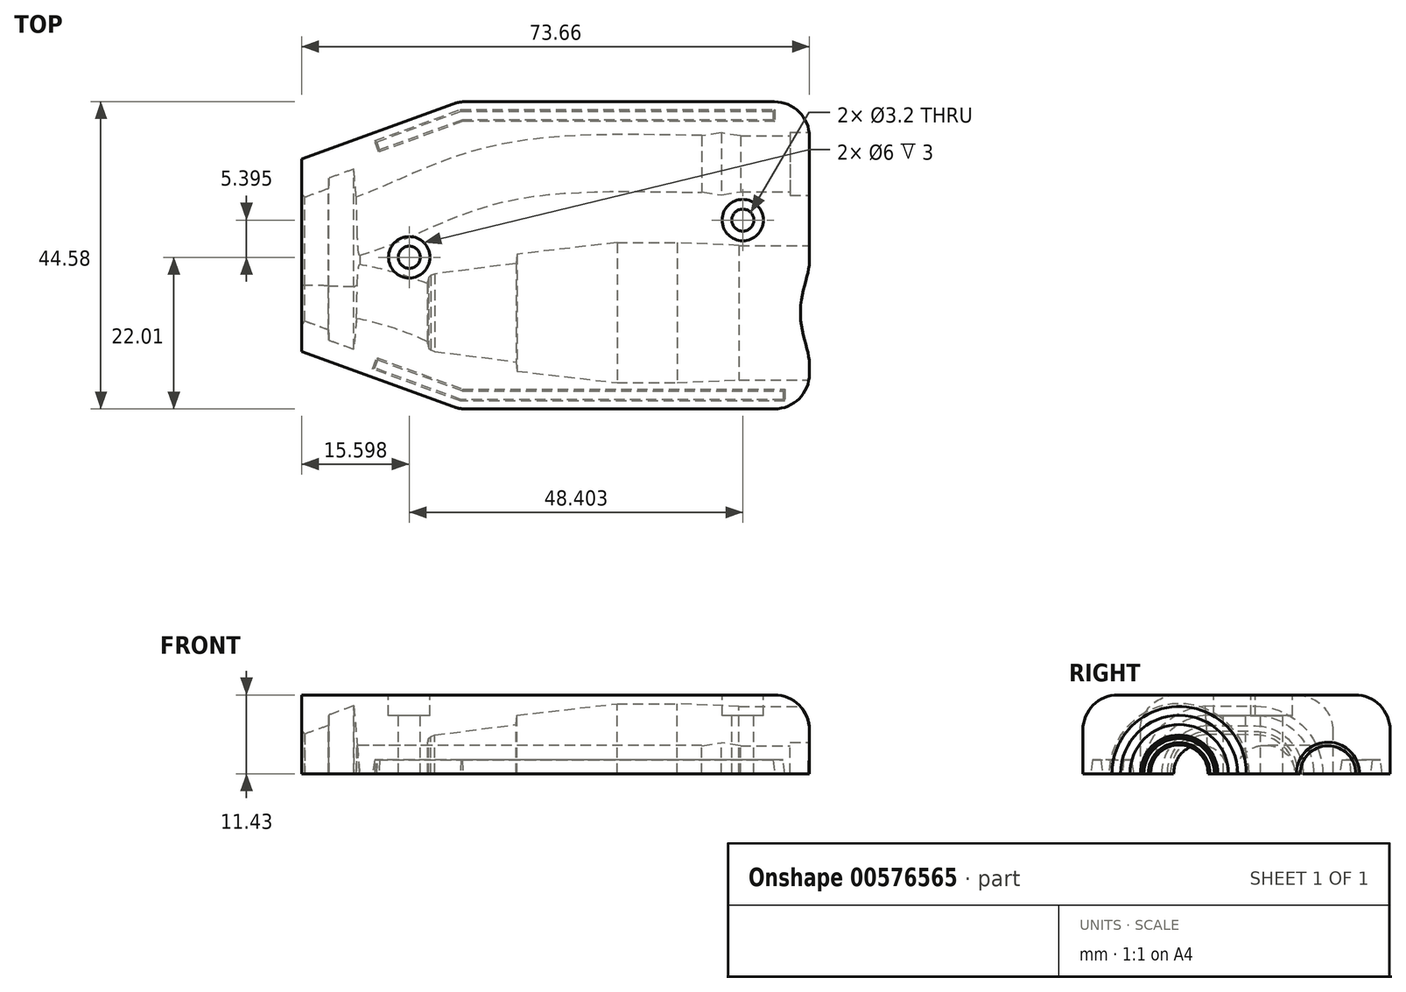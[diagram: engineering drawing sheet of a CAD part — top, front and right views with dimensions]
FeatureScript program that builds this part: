
annotation { "Feature Type Name" : "Feature", "Feature Type Description" : "" }
export const myFeature = defineFeature(function(context is Context, id is Id, definition is map)
    precondition{}
    {
        {
            var Q0;
            Q0=qCreatedBy(makeId("Top.planeOp"),FACE);
            var sketch = newSketch(context, id + "F0", { "sketchPlane" : qUnion([Q0])});
            skLineSegment(sketch, "E0", {"start": v(-29.16, 2.44) * mm, "end": v(45.25, 2.44) * mm});
            skLineSegment(sketch, "E1", {"start": v(45.25, 2.44) * mm, "end": v(45.25, -7.31) * mm});
            skLineSegment(sketch, "E2", {"start": v(45.25, -7.31) * mm, "end": v(33.01, -7.3) * mm});
            skLineSegment(sketch, "E3", {"start": v(33.01, -7.3) * mm, "end": v(31, -7.31) * mm});
            skLineSegment(sketch, "E4", {"start": v(31, -7.31) * mm, "end": v(16, -7.31) * mm});
            skLineSegment(sketch, "E5", {"start": v(16, -7.31) * mm, "end": v(7, -7.72) * mm});
            skLineSegment(sketch, "E6", {"start": v(7, -7.72) * mm, "end": v(-1.71, -7.72) * mm});
            skLineSegment(sketch, "E7", {"start": v(-1.71, -7.72) * mm, "end": v(-16.21, -6.04) * mm});
            skLineSegment(sketch, "E8", {"start": v(-16.21, -6.04) * mm, "end": v(-16.37, -4.7) * mm});
            skLineSegment(sketch, "E9", {"start": v(-16.37, -4.7) * mm, "end": v(-28.19, -3.17) * mm});
            skLineSegment(sketch, "E10", {"start": v(-28.19, -3.17) * mm, "end": v(-28.73, -2.96) * mm});
            skLineSegment(sketch, "E11", {"start": v(-28.73, -2.96) * mm, "end": v(-29.03, -2.68) * mm});
            skLineSegment(sketch, "E12", {"start": v(-29.03, -2.68) * mm, "end": v(-29.18, -2.06) * mm});
            skLineSegment(sketch, "E13", {"start": v(-29.18, -2.06) * mm, "end": v(-29.16, 2.44) * mm});
            skLineSegment(sketch, "E14.top", {"start": v(29.2, 18.83) * mm, "end": v(41.5, 18.83) * mm});
            skLineSegment(sketch, "E14.right", {"start": v(41.5, 24.03) * mm, "end": v(41.5, 18.83) * mm});
            skLineSegment(sketch, "E15", {"start": v(29.2, 19.46) * mm, "end": v(23.4, 19.46) * mm});
            skLineSegment(sketch, "E16", {"start": v(23.4, 19.46) * mm, "end": v(23.4, 24.03) * mm});
            skLineSegment(sketch, "E17", {"start": v(41.5, 24.03) * mm, "end": v(23.4, 24.03) * mm});
            skLineSegment(sketch, "E18", {"start": v(29.2, 18.83) * mm, "end": v(29.2, 19.46) * mm});
            skLineSegment(sketch, "E19.MirrorCS", {"start": v(-28.73, 7.85) * mm, "end": v(-29.03, 7.56) * mm});
            skLineSegment(sketch, "E20.MirrorCS", {"start": v(-29.03, 7.56) * mm, "end": v(-29.18, 6.94) * mm});
            skLineSegment(sketch, "E21.MirrorCS", {"start": v(33.01, 12.2) * mm, "end": v(31, 12.2) * mm});
            skLineSegment(sketch, "E22.MirrorCS", {"start": v(-28.19, 8.06) * mm, "end": v(-28.73, 7.85) * mm});
            skLineSegment(sketch, "E23.MirrorCS", {"start": v(-16.21, 10.93) * mm, "end": v(-16.37, 9.58) * mm});
            skLineSegment(sketch, "E24.MirrorCS", {"start": v(-16.37, 9.58) * mm, "end": v(-28.19, 8.06) * mm});
            skLineSegment(sketch, "E25.MirrorCS", {"start": v(7, 12.6) * mm, "end": v(-1.71, 12.6) * mm});
            skLineSegment(sketch, "E26.MirrorCS", {"start": v(45.25, 12.2) * mm, "end": v(33.01, 12.2) * mm});
            skLineSegment(sketch, "E27.MirrorCS", {"start": v(-1.71, 12.6) * mm, "end": v(-16.21, 10.93) * mm});
            skLineSegment(sketch, "E28.MirrorCS", {"start": v(16, 12.2) * mm, "end": v(7, 12.6) * mm});
            skLineSegment(sketch, "E29.MirrorCS", {"start": v(31, 12.2) * mm, "end": v(16, 12.2) * mm});
            skLineSegment(sketch, "E30.MirrorCS", {"start": v(45.25, 2.44) * mm, "end": v(45.25, 12.2) * mm});
            skLineSegment(sketch, "E31.MirrorCS", {"start": v(-29.18, 6.94) * mm, "end": v(-29.16, 2.44) * mm});
            skLineSegment(sketch, "E32", {"start": v(41.5, 20.03) * mm, "end": v(44.1, 20.03) * mm});
            skLineSegment(sketch, "E33", {"start": v(44.1, 20.03) * mm, "end": v(44.1, 24.03) * mm});
            skLineSegment(sketch, "E34", {"start": v(44.1, 24.03) * mm, "end": v(41.5, 24.03) * mm});
            skLineSegment(sketch, "E35", {"start": v(44.1, 20.03) * mm, "end": v(44.1, 19.46) * mm});
            skLineSegment(sketch, "E36", {"start": v(44.1, 19.46) * mm, "end": v(45.25, 19.46) * mm});
            skLineSegment(sketch, "E37", {"start": v(45.25, 19.46) * mm, "end": v(45.32, 24.03) * mm});
            skLineSegment(sketch, "E38", {"start": v(45.32, 24.03) * mm, "end": v(44.1, 24.03) * mm});
            skLineSegment(sketch, "E39", {"start": v(23.4, 24.03) * mm, "end": v(16.2, 24.03) * mm});
            skLineSegment(sketch, "E40", {"start": v(16.2, 24.03) * mm, "end": v(16.2, 19.98) * mm});
            skLineSegment(sketch, "E41", {"start": v(16.2, 19.98) * mm, "end": v(23.4, 19.98) * mm});
            skLineSegment(sketch, "E42", {"start": v(16.2, 19.98) * mm, "end": v(13.4, 19.53) * mm});
            skLineSegment(sketch, "E43", {"start": v(13.4, 19.53) * mm, "end": v(10.6, 19.98) * mm});
            skLineSegment(sketch, "E44", {"start": v(10.6, 19.98) * mm, "end": v(10.6, 24.03) * mm});
            skLineSegment(sketch, "E45", {"start": v(10.6, 24.03) * mm, "end": v(16.2, 24.03) * mm});
            skLineSegment(sketch, "E46.MirrorCS", {"start": v(44.1, 28.03) * mm, "end": v(44.1, 28.6) * mm});
            skLineSegment(sketch, "E47.MirrorCS", {"start": v(44.1, 28.6) * mm, "end": v(45.25, 28.6) * mm});
            skLineSegment(sketch, "E48.MirrorCS", {"start": v(29.2, 29.24) * mm, "end": v(29.2, 28.6) * mm});
            skLineSegment(sketch, "E49.MirrorCS", {"start": v(44.1, 28.03) * mm, "end": v(44.1, 24.03) * mm});
            skLineSegment(sketch, "E50.MirrorCS", {"start": v(16.2, 24.03) * mm, "end": v(16.2, 28.08) * mm});
            skLineSegment(sketch, "E51.MirrorCS", {"start": v(23.4, 28.6) * mm, "end": v(23.4, 24.03) * mm});
            skLineSegment(sketch, "E52.MirrorCS", {"start": v(10.6, 28.08) * mm, "end": v(10.6, 24.03) * mm});
            skLineSegment(sketch, "E53.MirrorCS", {"start": v(29.2, 28.6) * mm, "end": v(23.4, 28.6) * mm});
            skLineSegment(sketch, "E54.MirrorCS", {"start": v(41.5, 24.03) * mm, "end": v(41.5, 29.24) * mm});
            skLineSegment(sketch, "E55.MirrorCS", {"start": v(29.2, 29.24) * mm, "end": v(41.5, 29.24) * mm});
            skLineSegment(sketch, "E56.MirrorCS", {"start": v(45.25, 28.6) * mm, "end": v(45.32, 24.03) * mm});
            skLineSegment(sketch, "E57.MirrorCS", {"start": v(13.4, 28.53) * mm, "end": v(10.6, 28.08) * mm});
            skLineSegment(sketch, "E58.MirrorCS", {"start": v(41.5, 28.03) * mm, "end": v(44.1, 28.03) * mm});
            skLineSegment(sketch, "E59.MirrorCS", {"start": v(16.2, 28.08) * mm, "end": v(13.4, 28.53) * mm});
            skLineSegment(sketch, "E60.MirrorCS", {"start": v(16.2, 28.08) * mm, "end": v(23.4, 28.08) * mm});
            skSolve(sketch);
        }
        {
            var Q0;
            Q0=qCreatedBy(makeId("Top.planeOp"),FACE);
            var sketch = newSketch(context, id + "F1", { "sketchPlane" : qUnion([Q0])});
            skLineSegment(sketch, "E61.0", {"start": v(45.25, 2.44) * mm, "end": v(45.25, -7.31) * mm});
            skLineSegment(sketch, "E62", {"start": v(26.2, 33.05) * mm, "end": v(26.2, -11.53) * mm});
            skLineSegment(sketch, "E63", {"start": v(26.2, -11.53) * mm, "end": v(-24.6, -11.53) * mm});
            skLineSegment(sketch, "E64", {"start": v(-24.6, -11.53) * mm, "end": v(-47.46, -3.2) * mm});
            skLineSegment(sketch, "E65", {"start": v(-47.46, -3.2) * mm, "end": v(-47.46, 24.73) * mm});
            skLineSegment(sketch, "E66", {"start": v(-47.46, 24.73) * mm, "end": v(-24.6, 33.05) * mm});
            skLineSegment(sketch, "E67", {"start": v(-24.6, 33.05) * mm, "end": v(26.2, 33.05) * mm});
            skLineSegment(sketch, "E68.0", {"start": v(29.2, 29.24) * mm, "end": v(41.5, 29.24) * mm});
            skSolve(sketch);
        }
        {
            var Q0;
            Q0=qSketchRegion(id+"F1",true);
            extrude(context, id + "F2", {"entities" : qUnion([Q0]), "oppositeDirection" : true, "depth" : 0 * mm, "offsetDistance" : 25.4 * mm, "hasSecondDirection" : true, "secondDirectionOppositeDirection" : false, "secondDirectionDepth" : 11.43 * mm});
        }
        {
            var Q0;
            Q0=makeQuery(id+"F0.imprint","IMPRINT",FACE,{"disambiguationData":[TD([[makeQuery(id+"F0.imprint","IMPRINT",EDGE,{"derivedFrom":sQuery(id+"F0.wireOp",EDGE,"E0")}),-1.0]])]});
            var Q1;
            Q1=sQuery(id+"F0.wireOp",EDGE,"E0");
            revolve(context, id + "F3", {"operationType" : NewBodyOperationType.REMOVE, "entities" : qUnion([Q0]), "axis" : qUnion([Q1]), "revolveType" : RevolveType.FULL, "oppositeDirection" : true});
        }
        {
            var Q0;
            Q0=makeQuery(id+"F0.imprint","IMPRINT",FACE,{"disambiguationData":[TD([[makeQuery(id+"F0.imprint","IMPRINT",EDGE,{"derivedFrom":sQuery(id+"F0.wireOp",EDGE,"E14.top")}),1.0]])]});
            var Q1;
            Q1=makeQuery(id+"F0.imprint","IMPRINT",FACE,{"disambiguationData":[TD([[makeQuery(id+"F0.imprint","IMPRINT",EDGE,{"derivedFrom":sQuery(id+"F0.wireOp",EDGE,"E40")}),1.0]])]});
            var Q2;
            Q2=makeQuery(id+"F0.imprint","IMPRINT",FACE,{"disambiguationData":[TD([[makeQuery(id+"F0.imprint","IMPRINT",EDGE,{"derivedFrom":sQuery(id+"F0.wireOp",EDGE,"E40")}),-1.0]])]});
            var Q3;
            Q3=sQuery(id+"F0.wireOp",EDGE,"E17");
            revolve(context, id + "F4", {"operationType" : NewBodyOperationType.REMOVE, "entities" : qUnion([Q0, Q1, Q2]), "axis" : qUnion([Q3]), "revolveType" : RevolveType.FULL});
        }
        {
            var Q0;
            Q0=makeQuery(id+"F2.opExtrude","CAP_FACE",FACE,{"disambiguationData":[OSD([sQuery(id+"F1.wireOp",EDGE,"FN9DgEXL-DUnT-EqR8-ggIH-wTex11pTKOJ6"),sQuery(id+"F1.wireOp",EDGE,"Mmaicck8-LA38-ALDy-QV3c-pMFCgAv4KP83"),sQuery(id+"F1.wireOp",EDGE,"E62"),sQuery(id+"F1.wireOp",EDGE,"E63"),sQuery(id+"F1.wireOp",EDGE,"E64"),sQuery(id+"F1.wireOp",EDGE,"E65"),sQuery(id+"F1.wireOp",EDGE,"E66"),sQuery(id+"F1.wireOp",EDGE,"E67")])],"isStart":true});
            var sketch = newSketch(context, id + "F5", { "sketchPlane" : qUnion([Q0])});
            skLineSegment(sketch, "E69.0", {"start": v(-29.16, 2.44) * mm, "end": v(45.25, 2.44) * mm});
            skFitSpline(sketch, "E70", {"points": [v(-29.16, 2.44) * mm, v(-47.46, 6.7) * mm, v(-83.77, 9.93) * mm], "startDerivative": vector(-48.46, 20.5) * mm, "endDerivative": vector(-77.25, 2.74) * mm});
            skSolve(sketch);
        }
        {
            var Q0;
            Q0=sQuery(id+"F5.wireOp",VERTEX,"E70.0.internal");
            var Q1;
            Q1=sQuery(id+"F5.wireOp",EDGE,"E69.0");
            cPlane(context, id + "F6", {"entities" : qUnion([Q0, Q1]), "cplaneType" : CPlaneType.LINE_POINT, "offset" : 25.4 * mm, "width" : 152.4 * mm, "height" : 152.4 * mm});
        }
        {
            var Q0;
            Q0=qCreatedBy(id+"F6.planeOp",FACE);
            var sketch = newSketch(context, id + "F7", { "sketchPlane" : qUnion([Q0])});
            skCircle(sketch, "E71", {"center": v(2.44, 0) * mm, "radius": 4.2 * mm});
            skSolve(sketch);
        }
        {
            var Q0;
            Q0=qSketchRegion(id+"F7",true);
            var Q1;
            Q1=sQuery(id+"F5.wireOp",EDGE,"E70");
            sweep(context, id + "F8", {"operationType" : NewBodyOperationType.REMOVE, "profiles" : qUnion([Q0]), "path" : qUnion([Q1])});
        }
        {
            var Q0;
            Q0=sQuery(id+"F0.wireOp",VERTEX,"E45.start");
            var Q1;
            Q1=sQuery(id+"F0.wireOp",EDGE,"E45");
            cPlane(context, id + "F9", {"entities" : qUnion([Q0, Q1]), "cplaneType" : CPlaneType.LINE_POINT, "offset" : 25.4 * mm, "width" : 152.4 * mm, "height" : 152.4 * mm});
        }
        {
            var Q0;
            {var subQ0=sQuery(id+"F1.wireOp",EDGE,"E62");var subQ1=sQuery(id+"F1.wireOp",EDGE,"E65");var subQ2=sQuery(id+"F1.wireOp",EDGE,"E66");var subQ3=sQuery(id+"F1.wireOp",EDGE,"E67");Q0=makeQuery(id+"F8.boolean.opBoolean","SPLIT",FACE,{"disambiguationData":[TD([makeQuery(id+"F2.opExtrude","SWEPT_FACE",FACE,{"disambiguationData":[OSD([subQ2])]})])],"derivedFrom":makeQuery(id+"F2.opExtrude","CAP_FACE",FACE,{"disambiguationData":[OSD([subQ0,sQuery(id+"F1.wireOp",EDGE,"E63"),sQuery(id+"F1.wireOp",EDGE,"E64"),subQ1,subQ2,subQ3])],"isStart":true})});}
            var sketch = newSketch(context, id + "F10", { "sketchPlane" : qUnion([Q0])});
            skLineSegment(sketch, "E72.0", {"start": v(10.6, 24.03) * mm, "end": v(16.2, 24.03) * mm});
            skFitSpline(sketch, "E73", {"points": [v(10.6, 24.03) * mm, v(-17.54, 22.88) * mm, v(-35.92, 16.19) * mm, v(-61.27, 13.83) * mm], "startDerivative": vector(-66.57, 0.28) * mm, "endDerivative": vector(-121.3, 10.88) * mm});
            skSolve(sketch);
        }
        {
            var Q0;
            Q0=qCreatedBy(id+"F9.planeOp",FACE);
            var sketch = newSketch(context, id + "F11", { "sketchPlane" : qUnion([Q0])});
            skCircle(sketch, "E74", {"center": v(24.03, 0) * mm, "radius": 4.12 * mm});
            skSolve(sketch);
        }
        {
            var Q0;
            Q0=qSketchRegion(id+"F11",true);
            var Q1;
            Q1=sQuery(id+"F10.wireOp",EDGE,"E73");
            sweep(context, id + "F12", {"operationType" : NewBodyOperationType.REMOVE, "profiles" : qUnion([Q0]), "path" : qUnion([Q1])});
        }
        {
            var Q0;
            Q0=qCreatedBy(makeId("Top.planeOp"),FACE);
            var sketch = newSketch(context, id + "F13", { "sketchPlane" : qUnion([Q0])});
            skLineSegment(sketch, "E75.0", {"start": v(-24.4, 31.92) * mm, "end": v(21.2, 31.92) * mm});
            skLineSegment(sketch, "E75.1", {"start": v(-36.88, 27.38) * mm, "end": v(-24.4, 31.92) * mm});
            skPoint(sketch, "E76", {"position": v(21.2, 31.92) * mm});
            skPoint(sketch, "E77", {"position": v(-36.88, 27.38) * mm});
            skLineSegment(sketch, "E78.0", {"start": v(-24.09, 30.17) * mm, "end": v(21.2, 30.17) * mm});
            skLineSegment(sketch, "E78.1", {"start": v(-36.28, 25.74) * mm, "end": v(-24.09, 30.17) * mm});
            skLineSegment(sketch, "E79", {"start": v(21.2, 30.17) * mm, "end": v(21.2, 31.92) * mm});
            skLineSegment(sketch, "E80", {"start": v(-36.88, 27.38) * mm, "end": v(-36.28, 25.74) * mm});
            skLineSegment(sketch, "E81.0", {"start": v(-24.4, -10.4) * mm, "end": v(-37.17, -5.75) * mm});
            skLineSegment(sketch, "E81.1", {"start": v(22.64, -10.4) * mm, "end": v(-24.4, -10.4) * mm});
            skPoint(sketch, "E82", {"position": v(22.64, -10.4) * mm});
            skPoint(sketch, "E83", {"position": v(-37.17, -5.75) * mm});
            skLineSegment(sketch, "E84.0", {"start": v(-24.09, -8.65) * mm, "end": v(-36.57, -4.1) * mm});
            skLineSegment(sketch, "E84.1", {"start": v(22.64, -8.65) * mm, "end": v(-24.09, -8.65) * mm});
            skLineSegment(sketch, "E85", {"start": v(22.64, -10.4) * mm, "end": v(22.64, -8.65) * mm});
            skLineSegment(sketch, "E86", {"start": v(-37.17, -5.75) * mm, "end": v(-36.57, -4.1) * mm});
            skSolve(sketch);
        }
        {
            var Q0;
            Q0=qSketchRegion(id+"F13",true);
            extrude(context, id + "F14", {"entities" : qUnion([Q0]), "operationType" : NewBodyOperationType.REMOVE, "depth" : 2 * mm, "offsetDistance" : 25.4 * mm, "hasDraft" : true, "draftAngle" : 7 * degree, "draftPullDirection" : true});
        }
        {
            var Q0;
            {var subQ4=sQuery(id+"F1.wireOp",EDGE,"E62");var subQ8=makeQuery(id+"F3.boolean.opBoolean","COPY",FACE,{"derivedFrom":makeQuery(id+"F3.opRevolve","SWEPT_FACE",FACE,{"disambiguationData":[OSD([sQuery(id+"F0.wireOp",EDGE,"E4")])]})});var subQ19=sQuery(id+"F1.wireOp",EDGE,"E65");var subQ20=sQuery(id+"F1.wireOp",EDGE,"E66");var subQ21=sQuery(id+"F1.wireOp",EDGE,"E67");Q0=makeQuery(id+"F12.boolean.opBoolean","SPLIT",FACE,{"disambiguationData":[TD([subQ8])],"derivedFrom":makeQuery(id+"F8.boolean.opBoolean","SPLIT",FACE,{"disambiguationData":[TD([makeQuery(id+"F2.opExtrude","SWEPT_FACE",FACE,{"disambiguationData":[OSD([subQ20])]})])],"derivedFrom":makeQuery(id+"F2.opExtrude","CAP_FACE",FACE,{"disambiguationData":[OSD([subQ4,sQuery(id+"F1.wireOp",EDGE,"E63"),sQuery(id+"F1.wireOp",EDGE,"E64"),subQ19,subQ20,subQ21])],"isStart":true})})});}
            var sketch = newSketch(context, id + "F15", { "sketchPlane" : qUnion([Q0])});
            skCircle(sketch, "E87", {"center": v(-31.86, 10.48) * mm, "radius": 1.6 * mm});
            skCircle(sketch, "E88", {"center": v(16.54, 15.88) * mm, "radius": 1.6 * mm});
            skSolve(sketch);
        }
        {
            var Q0;
            Q0=qSketchRegion(id+"F15",true);
            extrude(context, id + "F16", {"entities" : qUnion([Q0]), "operationType" : NewBodyOperationType.REMOVE, "oppositeDirection" : true, "depth" : 25.4 * mm, "offsetDistance" : 25.4 * mm});
        }
        {
            var Q0;
            Q0=makeQuery(id+"F2.opExtrude","SWEPT_FACE",FACE,{"disambiguationData":[OSD([sQuery(id+"F1.wireOp",EDGE,"E65")])]});
            var sketch = newSketch(context, id + "F17", { "sketchPlane" : qUnion([Q0])});
            skArc(sketch, "E89", {"start": v(-13.53, 4.12) * mm, "mid": v(-16.42, 2.9) * mm, "end": v(-17.6, 0) * mm});
            skArc(sketch, "E90", {"start": v(-2.8, 0) * mm, "mid": v(-3.85, 2.8) * mm, "end": v(-6.5, 4.19) * mm});
            skLineSegment(sketch, "E91", {"start": v(-13.53, 4.12) * mm, "end": v(-6.5, 4.19) * mm});
            skSolve(sketch);
        }
        {
            var Q0;
            Q0=qCreatedBy(makeId("Top.planeOp"),FACE);
            var sketch = newSketch(context, id + "F18", { "sketchPlane" : qUnion([Q0])});
            skLineSegment(sketch, "E92", {"start": v(-39.23, 4.74) * mm, "end": v(-39.9, -2.86) * mm});
            skLineSegment(sketch, "E93", {"start": v(-43.55, -1.54) * mm, "end": v(-43.57, -0.02) * mm});
            skLineSegment(sketch, "E94", {"start": v(-47, 1.23) * mm, "end": v(-49.56, -1.34) * mm});
            skLineSegment(sketch, "E95", {"start": v(-49.56, -1.34) * mm, "end": v(-50.55, 5.78) * mm});
            skLineSegment(sketch, "E96", {"start": v(-50.55, 5.78) * mm, "end": v(-39.23, 4.74) * mm});
            skLineSegment(sketch, "E97", {"start": v(-47, 1.23) * mm, "end": v(-43.57, -0.02) * mm});
            skLineSegment(sketch, "E98", {"start": v(-43.55, -1.54) * mm, "end": v(-39.9, -2.86) * mm});
            skSolve(sketch);
        }
        {
            var Q0;
            Q0=makeQuery(id+"F18.imprint","IMPRINT",FACE,{"disambiguationData":[TD([[makeQuery(id+"F18.imprint","IMPRINT",EDGE,{"derivedFrom":sQuery(id+"F18.wireOp",EDGE,"E92")}),-1.0]])]});
            var Q1;
            Q1=sQuery(id+"F17.wireOp",EDGE,"E91");
            var Q2;
            Q2=sQuery(id+"F17.wireOp",EDGE,"E89");
            var Q3;
            Q3=sQuery(id+"F17.wireOp",EDGE,"E90");
            sweep(context, id + "F19", {"operationType" : NewBodyOperationType.REMOVE, "profiles" : qUnion([Q0]), "path" : qUnion([Q1, Q2, Q3])});
        }
        {
            var Q0;
            Q0=makeQuery(id+"F19.boolean.opBoolean","COPY",FACE,{"derivedFrom":makeQuery(id+"F19.opSweep","SWEPT_FACE",FACE,{"disambiguationData":[OSD([sQuery(id+"F17.wireOp",EDGE,"E91"),sQuery(id+"F18.wireOp",EDGE,"E92")])]})});
            var sketch = newSketch(context, id + "F20", { "sketchPlane" : qUnion([Q0])});
            skLineSegment(sketch, "E99", {"start": v(-6.53, 7.51) * mm, "end": v(-13.56, 7.35) * mm});
            skLineSegment(sketch, "E100", {"start": v(-11.44, -0.76) * mm, "end": v(-13.56, 7.35) * mm});
            skLineSegment(sketch, "E101", {"start": v(-11.44, -0.76) * mm, "end": v(-9.45, -0.93) * mm});
            skLineSegment(sketch, "E102", {"start": v(-6.53, 7.51) * mm, "end": v(-9.45, -0.93) * mm});
            skSolve(sketch);
        }
        {
            var Q0;
            Q0=qSketchRegion(id+"F20",true);
            extrude(context, id + "F21", {"entities" : qUnion([Q0]), "operationType" : NewBodyOperationType.REMOVE, "depth" : 25.4 * mm, "offsetDistance" : 25.4 * mm});
        }
        {
            var Q0;
            Q0=makeQuery(id+"F2.opExtrude","CAP_EDGE",EDGE,{"disambiguationData":[OSD([sQuery(id+"F1.wireOp",EDGE,"E64")])],"isStart":true});
            var Q1;
            Q1=makeQuery(id+"F2.opExtrude","SWEPT_EDGE",EDGE,{"disambiguationData":[OSD([sQuery(id+"F1.wireOp",EDGE,"E63"),sQuery(id+"F1.wireOp",EDGE,"E64")])]});
            var Q2;
            Q2=makeQuery(id+"F2.opExtrude","CAP_EDGE",EDGE,{"disambiguationData":[OSD([sQuery(id+"F1.wireOp",EDGE,"E63")])],"isStart":true});
            var Q3;
            Q3=makeQuery(id+"F2.opExtrude","SWEPT_EDGE",EDGE,{"disambiguationData":[OSD([sQuery(id+"F1.wireOp",EDGE,"E62"),sQuery(id+"F1.wireOp",EDGE,"E63")])]});
            var Q4;
            Q4=makeQuery(id+"F2.opExtrude","CAP_EDGE",EDGE,{"disambiguationData":[OSD([sQuery(id+"F1.wireOp",EDGE,"E62")])],"isStart":true});
            var Q5;
            Q5=makeQuery(id+"F2.opExtrude","SWEPT_EDGE",EDGE,{"disambiguationData":[OSD([sQuery(id+"F1.wireOp",EDGE,"E62"),sQuery(id+"F1.wireOp",EDGE,"E67")])]});
            var Q6;
            Q6=makeQuery(id+"F2.opExtrude","CAP_EDGE",EDGE,{"disambiguationData":[OSD([sQuery(id+"F1.wireOp",EDGE,"E67")])],"isStart":true});
            var Q7;
            Q7=makeQuery(id+"F2.opExtrude","SWEPT_EDGE",EDGE,{"disambiguationData":[OSD([sQuery(id+"F1.wireOp",EDGE,"E66"),sQuery(id+"F1.wireOp",EDGE,"E67")])]});
            var Q8;
            Q8=makeQuery(id+"F2.opExtrude","CAP_EDGE",EDGE,{"disambiguationData":[OSD([sQuery(id+"F1.wireOp",EDGE,"E66")])],"isStart":true});
            fillet(context, id + "F22", {"entities" : qUnion([Q0, Q1, Q2, Q3, Q4, Q5, Q6, Q7, Q8]), "radius" : 5.08 * mm, "tangentPropagation" : true, "allowEdgeOverflow" : false});
        }
        {
            var Q0;
            Q0=makeQuery(id+"F2.opExtrude","CAP_FACE",FACE,{"disambiguationData":[OSD([sQuery(id+"F1.wireOp",EDGE,"E62"),sQuery(id+"F1.wireOp",EDGE,"E63"),sQuery(id+"F1.wireOp",EDGE,"E64"),sQuery(id+"F1.wireOp",EDGE,"E65"),sQuery(id+"F1.wireOp",EDGE,"E66"),sQuery(id+"F1.wireOp",EDGE,"E67")])],"isStart":true});
            var sketch = newSketch(context, id + "F23", { "sketchPlane" : qUnion([Q0])});
            skCircle(sketch, "E103", {"center": v(-31.86, 10.48) * mm, "radius": 3 * mm});
            skCircle(sketch, "E104", {"center": v(16.54, 15.88) * mm, "radius": 3 * mm});
            skSolve(sketch);
        }
        {
            var Q0;
            Q0 = qSketchRegion(id + "F23", true);
            extrude(context, id + "F24", {"entities" : qUnion([Q0]), "operationType" : NewBodyOperationType.REMOVE, "oppositeDirection" : true, "depth" : 3 * mm, "offsetDistance" : 25.4 * mm});
        }
    });
